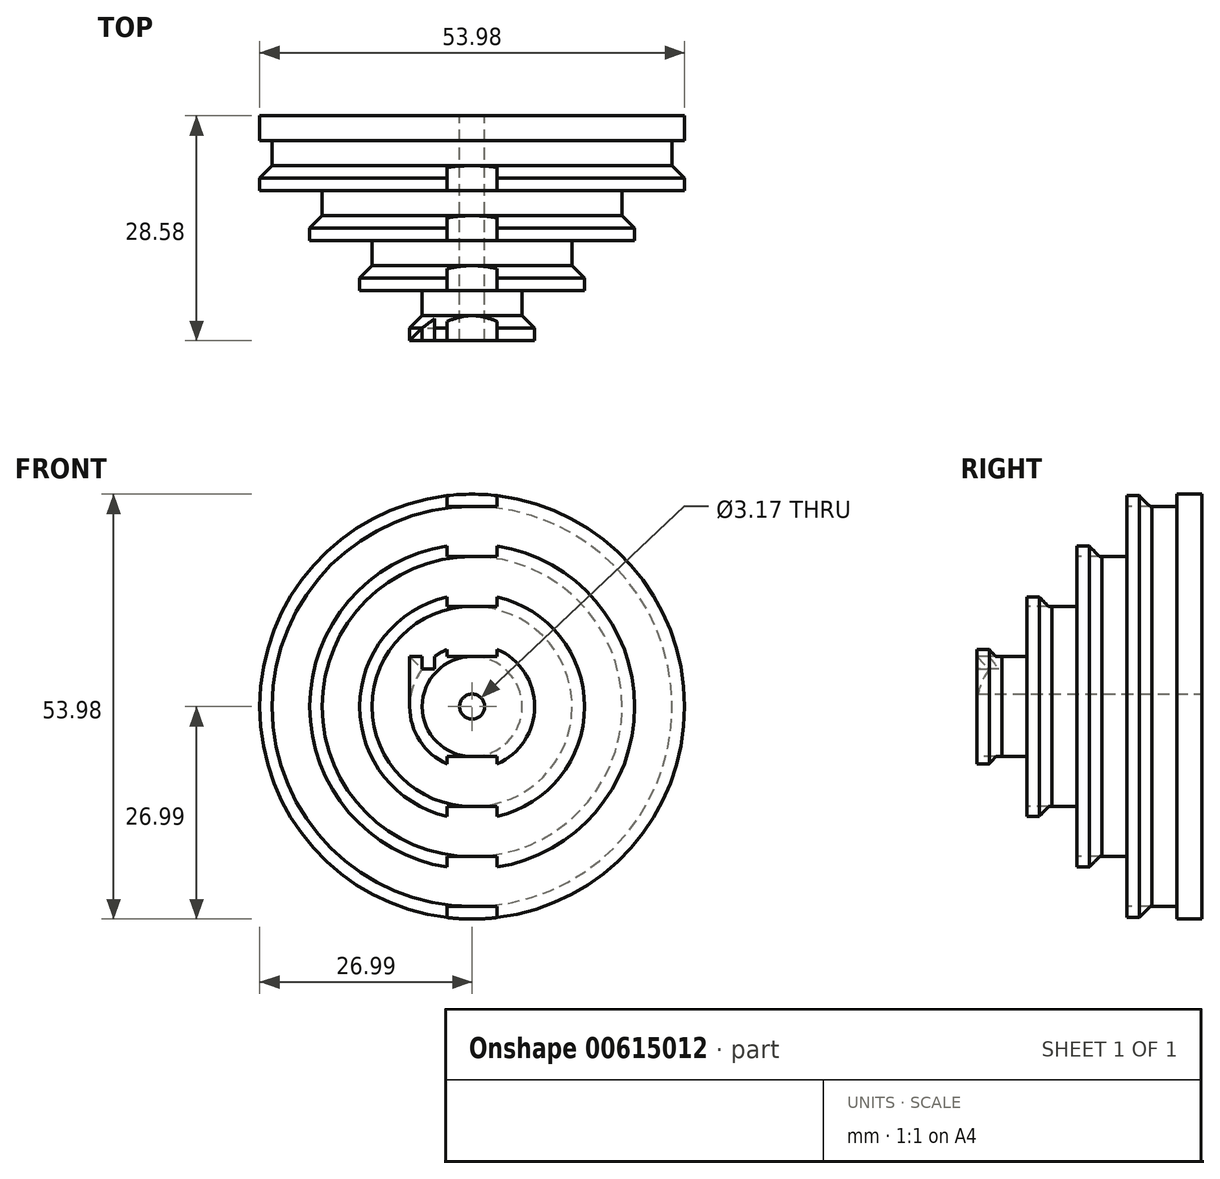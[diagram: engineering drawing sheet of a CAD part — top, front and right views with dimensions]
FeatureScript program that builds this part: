
annotation { "Feature Type Name" : "Feature", "Feature Type Description" : "" }
export const myFeature = defineFeature(function(context is Context, id is Id, definition is map)
    precondition{}
    {
        {
            var Q0;
            Q0=qCreatedBy(makeId("Front.planeOp"),FACE);
            var sketch = newSketch(context, id + "F0", { "sketchPlane" : qUnion([Q0])});
            skCircle(sketch, "E0", {"center": v(0, 0) * mm, "radius": 26.99 * mm});
            skSolve(sketch);
        }
        {
            var Q0;
            Q0=makeQuery(id+"F0.imprint","IMPRINT",FACE,{"disambiguationData":[TD([[makeQuery(id+"F0.imprint","IMPRINT",EDGE,{"derivedFrom":sQuery(id+"F0.wireOp",EDGE,"E0")}),1.0]])]});
            extrude(context, id + "F1", {"entities" : qUnion([Q0]), "depth" : 3.17 * mm, "offsetDistance" : 25.4 * mm});
        }
        {
            var Q0;
            Q0=makeQuery(id+"F1.opExtrude","CAP_FACE",FACE,{"disambiguationData":[OSD([sQuery(id+"F0.wireOp",EDGE,"E0")])],"isStart":false});
            var sketch = newSketch(context, id + "F2", { "sketchPlane" : qUnion([Q0])});
            skCircle(sketch, "E1", {"center": v(0, 0) * mm, "radius": 25.4 * mm});
            skSolve(sketch);
        }
        {
            var Q0;
            Q0=makeQuery(id+"F2.imprint","IMPRINT",FACE,{"disambiguationData":[TD([[makeQuery(id+"F2.imprint","IMPRINT",EDGE,{"derivedFrom":sQuery(id+"F2.wireOp",EDGE,"E1")}),1.0]])]});
            extrude(context, id + "F3", {"entities" : qUnion([Q0]), "operationType" : NewBodyOperationType.ADD, "depth" : 3.17 * mm, "offsetDistance" : 25.4 * mm});
        }
        {
            var Q0;
            Q0=makeQuery(id+"F3.opExtrude","CAP_FACE",FACE,{"disambiguationData":[OSD([sQuery(id+"F2.wireOp",EDGE,"E1")])],"isStart":false});
            var sketch = newSketch(context, id + "F4", { "sketchPlane" : qUnion([Q0])});
            skCircle(sketch, "E2", {"center": v(0, 0) * mm, "radius": 26.99 * mm});
            skSolve(sketch);
        }
        {
            var Q0;
            Q0=makeQuery(id+"F4.imprint","IMPRINT",FACE,{"disambiguationData":[TD([[makeQuery(id+"F4.imprint","IMPRINT",EDGE,{"derivedFrom":sQuery(id+"F4.wireOp",EDGE,"E2")}),1.0]])]});
            var Q1;
            Q1=makeQuery(id+"F4.imprint","IMPRINT",FACE,{"disambiguationData":[TD([[makeQuery(id+"F4.imprint","IMPRINT",EDGE,{"derivedFrom":makeQuery(id+"F3.opExtrude","CAP_EDGE",EDGE,{"disambiguationData":[OSD([sQuery(id+"F2.wireOp",EDGE,"E1")])],"isStart":false})}),1.0]])]});
            extrude(context, id + "F5", {"entities" : qUnion([Q0, Q1]), "operationType" : NewBodyOperationType.ADD, "depth" : 3.17 * mm, "offsetDistance" : 25.4 * mm});
        }
        {
            var Q0;
            Q0=makeQuery(id+"F5.opExtrude","CAP_FACE",FACE,{"disambiguationData":[OSD([sQuery(id+"F4.wireOp",EDGE,"E2")])],"isStart":false});
            var sketch = newSketch(context, id + "F6", { "sketchPlane" : qUnion([Q0])});
            skLineSegment(sketch, "E3.bottom", {"start": v(3.17, 25.4) * mm, "end": v(-3.18, 25.4) * mm});
            skLineSegment(sketch, "E3.top", {"start": v(3.17, 28.57) * mm, "end": v(-3.18, 28.57) * mm});
            skLineSegment(sketch, "E3.left", {"start": v(3.17, 25.4) * mm, "end": v(3.17, 28.57) * mm});
            skLineSegment(sketch, "E3.right", {"start": v(-3.18, 25.4) * mm, "end": v(-3.18, 28.57) * mm});
            skPoint(sketch, "E3.middle", {"position": v(0, 26.99) * mm});
            skSolve(sketch);
        }
        {
            var Q0;
            Q0 = qSketchRegion(id + "F6", true);
            extrude(context, id + "F7", {"entities" : qUnion([Q0]), "operationType" : NewBodyOperationType.REMOVE, "oppositeDirection" : true, "depth" : 3.17 * mm, "offsetDistance" : 25.4 * mm});
        }
        {
            var Q0;
            Q0=makeQuery(id+"F5.opExtrude","CAP_FACE",FACE,{"disambiguationData":[OSD([sQuery(id+"F4.wireOp",EDGE,"E2")])],"isStart":false});
            var sketch = newSketch(context, id + "F8", { "sketchPlane" : qUnion([Q0])});
            skCircle(sketch, "E4", {"center": v(0, 0) * mm, "radius": 19.05 * mm});
            skSolve(sketch);
        }
        {
            var Q0;
            Q0 = qSketchRegion(id + "F8", true);
            extrude(context, id + "F9", {"entities" : qUnion([Q0]), "operationType" : NewBodyOperationType.ADD, "depth" : 3.17 * mm, "offsetDistance" : 25.4 * mm});
        }
        {
            var Q0;
            Q0=makeQuery(id+"F9.opExtrude","CAP_FACE",FACE,{"disambiguationData":[OSD([sQuery(id+"F8.wireOp",EDGE,"E4")])],"isStart":false});
            var sketch = newSketch(context, id + "F10", { "sketchPlane" : qUnion([Q0])});
            skCircle(sketch, "E5", {"center": v(0, 0) * mm, "radius": 20.64 * mm});
            skSolve(sketch);
        }
        {
            var Q0;
            Q0 = qSketchRegion(id + "F10", true);
            extrude(context, id + "F11", {"entities" : qUnion([Q0]), "operationType" : NewBodyOperationType.ADD, "depth" : 3.17 * mm, "offsetDistance" : 25.4 * mm});
        }
        {
            var Q0;
            Q0=makeQuery(id+"F11.opExtrude","CAP_FACE",FACE,{"disambiguationData":[OSD([sQuery(id+"F10.wireOp",EDGE,"E5")])],"isStart":false});
            var sketch = newSketch(context, id + "F12", { "sketchPlane" : qUnion([Q0])});
            skLineSegment(sketch, "E6.bottom", {"start": v(3.18, 19.05) * mm, "end": v(-3.17, 19.05) * mm});
            skLineSegment(sketch, "E6.top", {"start": v(3.18, 22.23) * mm, "end": v(-3.17, 22.23) * mm});
            skLineSegment(sketch, "E6.left", {"start": v(3.18, 19.05) * mm, "end": v(3.18, 22.23) * mm});
            skLineSegment(sketch, "E6.right", {"start": v(-3.17, 19.05) * mm, "end": v(-3.17, 22.23) * mm});
            skPoint(sketch, "E6.middle", {"position": v(0, 20.64) * mm});
            skSolve(sketch);
        }
        {
            var Q0;
            Q0 = qSketchRegion(id + "F12", true);
            extrude(context, id + "F13", {"entities" : qUnion([Q0]), "operationType" : NewBodyOperationType.REMOVE, "oppositeDirection" : true, "depth" : 3.17 * mm, "offsetDistance" : 25.4 * mm});
        }
        {
            var Q0;
            Q0=makeQuery(id+"F5.opExtrude","CAP_FACE",FACE,{"disambiguationData":[OSD([sQuery(id+"F4.wireOp",EDGE,"E2")])],"isStart":false});
            var sketch = newSketch(context, id + "F14", { "sketchPlane" : qUnion([Q0])});
            skLineSegment(sketch, "E7.bottom", {"start": v(3.18, -25.4) * mm, "end": v(-3.17, -25.4) * mm});
            skLineSegment(sketch, "E7.top", {"start": v(3.18, -28.57) * mm, "end": v(-3.17, -28.57) * mm});
            skLineSegment(sketch, "E7.left", {"start": v(3.18, -25.4) * mm, "end": v(3.18, -28.57) * mm});
            skLineSegment(sketch, "E7.right", {"start": v(-3.17, -25.4) * mm, "end": v(-3.17, -28.57) * mm});
            skPoint(sketch, "E7.middle", {"position": v(0, -26.99) * mm});
            skSolve(sketch);
        }
        {
            var Q0;
            Q0 = qSketchRegion(id + "F14", true);
            extrude(context, id + "F15", {"entities" : qUnion([Q0]), "operationType" : NewBodyOperationType.REMOVE, "oppositeDirection" : true, "depth" : 3.17 * mm, "offsetDistance" : 25.4 * mm});
        }
        {
            var Q0;
            Q0=makeQuery(id+"F11.opExtrude","CAP_FACE",FACE,{"disambiguationData":[OSD([sQuery(id+"F10.wireOp",EDGE,"E5")])],"isStart":false});
            var sketch = newSketch(context, id + "F16", { "sketchPlane" : qUnion([Q0])});
            skLineSegment(sketch, "E8.bottom", {"start": v(3.18, -19.05) * mm, "end": v(-3.17, -19.05) * mm});
            skLineSegment(sketch, "E8.top", {"start": v(3.18, -22.23) * mm, "end": v(-3.17, -22.23) * mm});
            skLineSegment(sketch, "E8.left", {"start": v(3.18, -19.05) * mm, "end": v(3.18, -22.23) * mm});
            skLineSegment(sketch, "E8.right", {"start": v(-3.17, -19.05) * mm, "end": v(-3.17, -22.23) * mm});
            skPoint(sketch, "E8.middle", {"position": v(0, -20.64) * mm});
            skSolve(sketch);
        }
        {
            var Q0;
            Q0 = qSketchRegion(id + "F16", true);
            extrude(context, id + "F17", {"entities" : qUnion([Q0]), "operationType" : NewBodyOperationType.REMOVE, "oppositeDirection" : true, "depth" : 3.17 * mm, "offsetDistance" : 25.4 * mm});
        }
        {
            var Q0;
            Q0=makeQuery(id+"F11.opExtrude","CAP_FACE",FACE,{"disambiguationData":[OSD([sQuery(id+"F10.wireOp",EDGE,"E5")])],"isStart":false});
            var sketch = newSketch(context, id + "F18", { "sketchPlane" : qUnion([Q0])});
            skCircle(sketch, "E9", {"center": v(0, 0) * mm, "radius": 12.7 * mm});
            skSolve(sketch);
        }
        {
            var Q0;
            Q0 = qSketchRegion(id + "F18", true);
            extrude(context, id + "F19", {"entities" : qUnion([Q0]), "operationType" : NewBodyOperationType.ADD, "depth" : 3.17 * mm, "offsetDistance" : 25.4 * mm});
        }
        {
            var Q0;
            Q0=makeQuery(id+"F19.opExtrude","CAP_FACE",FACE,{"disambiguationData":[OSD([sQuery(id+"F18.wireOp",EDGE,"E9")])],"isStart":false});
            var sketch = newSketch(context, id + "F20", { "sketchPlane" : qUnion([Q0])});
            skCircle(sketch, "E10", {"center": v(0, 0) * mm, "radius": 14.29 * mm});
            skSolve(sketch);
        }
        {
            var Q0;
            Q0 = qSketchRegion(id + "F20", true);
            extrude(context, id + "F21", {"entities" : qUnion([Q0]), "operationType" : NewBodyOperationType.ADD, "depth" : 3.17 * mm, "offsetDistance" : 25.4 * mm});
        }
        {
            var Q0;
            Q0=makeQuery(id+"F21.opExtrude","CAP_FACE",FACE,{"disambiguationData":[OSD([sQuery(id+"F20.wireOp",EDGE,"E10")])],"isStart":false});
            var sketch = newSketch(context, id + "F22", { "sketchPlane" : qUnion([Q0])});
            skLineSegment(sketch, "E11.bottom", {"start": v(3.17, 15.88) * mm, "end": v(-3.18, 15.88) * mm});
            skLineSegment(sketch, "E11.top", {"start": v(3.17, 12.7) * mm, "end": v(-3.18, 12.7) * mm});
            skLineSegment(sketch, "E11.left", {"start": v(3.17, 15.88) * mm, "end": v(3.17, 12.7) * mm});
            skLineSegment(sketch, "E11.right", {"start": v(-3.18, 15.88) * mm, "end": v(-3.18, 12.7) * mm});
            skPoint(sketch, "E11.middle", {"position": v(0, 14.29) * mm});
            skSolve(sketch);
        }
        {
            var Q0;
            Q0 = qSketchRegion(id + "F22", true);
            extrude(context, id + "F23", {"entities" : qUnion([Q0]), "operationType" : NewBodyOperationType.REMOVE, "oppositeDirection" : true, "depth" : 3.17 * mm, "offsetDistance" : 25.4 * mm});
        }
        {
            var Q0;
            Q0=makeQuery(id+"F21.opExtrude","CAP_FACE",FACE,{"disambiguationData":[OSD([sQuery(id+"F20.wireOp",EDGE,"E10")])],"isStart":false});
            var sketch = newSketch(context, id + "F24", { "sketchPlane" : qUnion([Q0])});
            skLineSegment(sketch, "E12.bottom", {"start": v(3.18, -12.7) * mm, "end": v(-3.17, -12.7) * mm});
            skLineSegment(sketch, "E12.top", {"start": v(3.18, -15.88) * mm, "end": v(-3.17, -15.88) * mm});
            skLineSegment(sketch, "E12.left", {"start": v(3.18, -12.7) * mm, "end": v(3.18, -15.88) * mm});
            skLineSegment(sketch, "E12.right", {"start": v(-3.17, -12.7) * mm, "end": v(-3.17, -15.88) * mm});
            skPoint(sketch, "E12.middle", {"position": v(0, -14.29) * mm});
            skSolve(sketch);
        }
        {
            var Q0;
            Q0 = qSketchRegion(id + "F24", true);
            extrude(context, id + "F25", {"entities" : qUnion([Q0]), "operationType" : NewBodyOperationType.REMOVE, "oppositeDirection" : true, "depth" : 3.17 * mm, "offsetDistance" : 25.4 * mm});
        }
        {
            var Q0;
            Q0=makeQuery(id+"F21.opExtrude","CAP_FACE",FACE,{"disambiguationData":[OSD([sQuery(id+"F20.wireOp",EDGE,"E10")])],"isStart":false});
            var sketch = newSketch(context, id + "F26", { "sketchPlane" : qUnion([Q0])});
            skCircle(sketch, "E13", {"center": v(0, 0) * mm, "radius": 6.35 * mm});
            skSolve(sketch);
        }
        {
            var Q0;
            Q0 = qSketchRegion(id + "F26", true);
            extrude(context, id + "F27", {"entities" : qUnion([Q0]), "operationType" : NewBodyOperationType.ADD, "depth" : 3.17 * mm, "offsetDistance" : 25.4 * mm});
        }
        {
            var Q0;
            Q0=makeQuery(id+"F27.opExtrude","CAP_FACE",FACE,{"disambiguationData":[OSD([sQuery(id+"F26.wireOp",EDGE,"E13")])],"isStart":false});
            var sketch = newSketch(context, id + "F28", { "sketchPlane" : qUnion([Q0])});
            skCircle(sketch, "E14", {"center": v(0, 0) * mm, "radius": 7.94 * mm});
            skSolve(sketch);
        }
        {
            var Q0;
            Q0 = qSketchRegion(id + "F28", true);
            extrude(context, id + "F29", {"entities" : qUnion([Q0]), "operationType" : NewBodyOperationType.ADD, "depth" : 3.17 * mm, "offsetDistance" : 25.4 * mm});
        }
        {
            var Q0;
            Q0=makeQuery(id+"F29.opExtrude","CAP_FACE",FACE,{"disambiguationData":[OSD([sQuery(id+"F28.wireOp",EDGE,"E14")])],"isStart":false});
            var sketch = newSketch(context, id + "F30", { "sketchPlane" : qUnion([Q0])});
            skLineSegment(sketch, "E15.bottom", {"start": v(3.17, 6.35) * mm, "end": v(-3.18, 6.35) * mm});
            skLineSegment(sketch, "E15.top", {"start": v(3.18, 9.53) * mm, "end": v(-3.17, 9.53) * mm});
            skLineSegment(sketch, "E15.left", {"start": v(3.17, 6.35) * mm, "end": v(3.18, 9.53) * mm});
            skLineSegment(sketch, "E15.right", {"start": v(-3.18, 6.35) * mm, "end": v(-3.17, 9.53) * mm});
            skPoint(sketch, "E15.middle", {"position": v(0, 7.94) * mm});
            skSolve(sketch);
        }
        {
            var Q0;
            Q0 = qSketchRegion(id + "F30", true);
            extrude(context, id + "F31", {"entities" : qUnion([Q0]), "operationType" : NewBodyOperationType.REMOVE, "oppositeDirection" : true, "depth" : 3.17 * mm, "offsetDistance" : 25.4 * mm});
        }
        {
            var Q0;
            Q0=makeQuery(id+"F29.opExtrude","CAP_FACE",FACE,{"disambiguationData":[OSD([sQuery(id+"F28.wireOp",EDGE,"E14")])],"isStart":false});
            var sketch = newSketch(context, id + "F32", { "sketchPlane" : qUnion([Q0])});
            skLineSegment(sketch, "E16.bottom", {"start": v(3.18, -6.35) * mm, "end": v(-3.17, -6.35) * mm});
            skLineSegment(sketch, "E16.top", {"start": v(3.18, -9.53) * mm, "end": v(-3.17, -9.53) * mm});
            skLineSegment(sketch, "E16.left", {"start": v(3.18, -6.35) * mm, "end": v(3.18, -9.53) * mm});
            skLineSegment(sketch, "E16.right", {"start": v(-3.17, -6.35) * mm, "end": v(-3.17, -9.53) * mm});
            skPoint(sketch, "E16.middle", {"position": v(0, -7.94) * mm});
            skSolve(sketch);
        }
        {
            var Q0;
            Q0 = qSketchRegion(id + "F32", true);
            extrude(context, id + "F33", {"entities" : qUnion([Q0]), "operationType" : NewBodyOperationType.REMOVE, "oppositeDirection" : true, "depth" : 3.17 * mm, "offsetDistance" : 25.4 * mm});
        }
        {
            var Q0;
            Q0=makeQuery(id+"F1.opExtrude","CAP_FACE",FACE,{"disambiguationData":[OSD([sQuery(id+"F0.wireOp",EDGE,"E0")])],"isStart":true});
            var sketch = newSketch(context, id + "F34", { "sketchPlane" : qUnion([Q0])});
            skCircle(sketch, "E17", {"center": v(0, 0) * mm, "radius": 1.59 * mm});
            skSolve(sketch);
        }
        {
            var Q0;
            Q0 = qSketchRegion(id + "F34", true);
            extrude(context, id + "F35", {"entities" : qUnion([Q0]), "operationType" : NewBodyOperationType.REMOVE, "oppositeDirection" : true, "depth" : 28.57 * mm, "offsetDistance" : 25.4 * mm});
        }
        {
            var Q0;
            {var subQ0=sQuery(id+"F4.wireOp",EDGE,"E2");Q0=makeQuery(id+"F15.boolean.opBoolean","SPLIT",EDGE,{"disambiguationData":[TD([makeQuery(id+"F7.boolean.opBoolean","COPY",FACE,{"derivedFrom":makeQuery(id+"F7.opExtrude","SWEPT_FACE",FACE,{"disambiguationData":[OSD([sQuery(id+"F6.wireOp",EDGE,"E3.left")])]})})])],"derivedFrom":makeQuery(id+"F5.opExtrude","CAP_EDGE",EDGE,{"disambiguationData":[OSD([subQ0])],"isStart":true})});}
            var Q1;
            {var subQ0=sQuery(id+"F4.wireOp",EDGE,"E2");Q1=makeQuery(id+"F15.boolean.opBoolean","SPLIT",EDGE,{"disambiguationData":[TD([makeQuery(id+"F7.boolean.opBoolean","COPY",FACE,{"derivedFrom":makeQuery(id+"F7.opExtrude","SWEPT_FACE",FACE,{"disambiguationData":[OSD([sQuery(id+"F6.wireOp",EDGE,"E3.right")])]})})])],"derivedFrom":makeQuery(id+"F5.opExtrude","CAP_EDGE",EDGE,{"disambiguationData":[OSD([subQ0])],"isStart":true})});}
            var Q2;
            {var subQ0=sQuery(id+"F10.wireOp",EDGE,"E5");Q2=makeQuery(id+"F17.boolean.opBoolean","SPLIT",EDGE,{"disambiguationData":[TD([makeQuery(id+"F13.boolean.opBoolean","COPY",FACE,{"derivedFrom":makeQuery(id+"F13.opExtrude","SWEPT_FACE",FACE,{"disambiguationData":[OSD([sQuery(id+"F12.wireOp",EDGE,"E6.left")])]})})])],"derivedFrom":makeQuery(id+"F11.opExtrude","CAP_EDGE",EDGE,{"disambiguationData":[OSD([subQ0])],"isStart":true})});}
            var Q3;
            {var subQ0=sQuery(id+"F10.wireOp",EDGE,"E5");Q3=makeQuery(id+"F17.boolean.opBoolean","SPLIT",EDGE,{"disambiguationData":[TD([makeQuery(id+"F13.boolean.opBoolean","COPY",FACE,{"derivedFrom":makeQuery(id+"F13.opExtrude","SWEPT_FACE",FACE,{"disambiguationData":[OSD([sQuery(id+"F12.wireOp",EDGE,"E6.right")])]})})])],"derivedFrom":makeQuery(id+"F11.opExtrude","CAP_EDGE",EDGE,{"disambiguationData":[OSD([subQ0])],"isStart":true})});}
            chamfer(context, id + "F36", {"entities" : qUnion([Q0, Q1, Q2, Q3]), "width" : 1.59 * mm, "tangentPropagation" : true});
        }
        {
            var Q0;
            Q0=makeQuery(id+"F29.opExtrude","CAP_FACE",FACE,{"disambiguationData":[OSD([sQuery(id+"F28.wireOp",EDGE,"E14")])],"isStart":false});
            var sketch = newSketch(context, id + "F37", { "sketchPlane" : qUnion([Q0])});
            skLineSegment(sketch, "E18.bottom", {"start": v(-7.94, 0) * mm, "end": v(-6.35, 0) * mm});
            skLineSegment(sketch, "E18.top", {"start": v(-7.94, 6.35) * mm, "end": v(-6.35, 6.35) * mm});
            skLineSegment(sketch, "E18.left", {"start": v(-7.94, 0) * mm, "end": v(-7.94, 6.35) * mm});
            skLineSegment(sketch, "E18.right", {"start": v(-6.35, 0) * mm, "end": v(-6.35, 6.35) * mm});
            skSolve(sketch);
        }
        {
            var Q0;
            Q0 = qSketchRegion(id + "F37", true);
            extrude(context, id + "F38", {"entities" : qUnion([Q0]), "operationType" : NewBodyOperationType.ADD, "oppositeDirection" : true, "depth" : 1.59 * mm, "offsetDistance" : 25.4 * mm});
        }
        {
            var Q0;
            {var subQ0=sQuery(id+"F20.wireOp",EDGE,"E10");Q0=makeQuery(id+"F25.boolean.opBoolean","SPLIT",EDGE,{"disambiguationData":[TD([makeQuery(id+"F23.boolean.opBoolean","COPY",FACE,{"derivedFrom":makeQuery(id+"F23.opExtrude","SWEPT_FACE",FACE,{"disambiguationData":[OSD([sQuery(id+"F22.wireOp",EDGE,"E11.right")])]})})])],"derivedFrom":makeQuery(id+"F21.opExtrude","CAP_EDGE",EDGE,{"disambiguationData":[OSD([subQ0])],"isStart":true})});}
            var Q1;
            {var subQ0=sQuery(id+"F20.wireOp",EDGE,"E10");Q1=makeQuery(id+"F25.boolean.opBoolean","SPLIT",EDGE,{"disambiguationData":[TD([makeQuery(id+"F23.boolean.opBoolean","COPY",FACE,{"derivedFrom":makeQuery(id+"F23.opExtrude","SWEPT_FACE",FACE,{"disambiguationData":[OSD([sQuery(id+"F22.wireOp",EDGE,"E11.left")])]})})])],"derivedFrom":makeQuery(id+"F21.opExtrude","CAP_EDGE",EDGE,{"disambiguationData":[OSD([subQ0])],"isStart":true})});}
            var Q2;
            {var subQ0=sQuery(id+"F28.wireOp",EDGE,"E14");Q2=makeQuery(id+"F33.boolean.opBoolean","SPLIT",EDGE,{"disambiguationData":[TD([makeQuery(id+"F31.boolean.opBoolean","COPY",FACE,{"derivedFrom":makeQuery(id+"F31.opExtrude","SWEPT_FACE",FACE,{"disambiguationData":[OSD([sQuery(id+"F30.wireOp",EDGE,"E15.left")])]})})])],"derivedFrom":makeQuery(id+"F29.opExtrude","CAP_EDGE",EDGE,{"disambiguationData":[OSD([subQ0])],"isStart":true})});}
            chamfer(context, id + "F39", {"entities" : qUnion([Q0, Q1, Q2]), "width" : 1.59 * mm, "tangentPropagation" : true});
        }
        {
            var Q0;
            Q0=makeQuery(id+"F38.boolean.opBoolean","MERGE",FACE,{"derivedFrom":[makeQuery(id+"F29.opExtrude","CAP_FACE",FACE,{"disambiguationData":[OSD([sQuery(id+"F28.wireOp",EDGE,"E14")])],"isStart":false}),makeQuery(id+"F38.opExtrude","CAP_FACE",FACE,{"disambiguationData":[OSD([sQuery(id+"F37.wireOp",EDGE,"E18.bottom"),sQuery(id+"F37.wireOp",EDGE,"E18.top"),sQuery(id+"F37.wireOp",EDGE,"E18.left"),sQuery(id+"F37.wireOp",EDGE,"E18.right")])],"isStart":true})]});
            var sketch = newSketch(context, id + "F40", { "sketchPlane" : qUnion([Q0])});
            skLineSegment(sketch, "E19.bottom", {"start": v(-6.35, 6.35) * mm, "end": v(-4.76, 6.35) * mm});
            skLineSegment(sketch, "E19.top", {"start": v(-6.35, 4.76) * mm, "end": v(-4.76, 4.76) * mm});
            skLineSegment(sketch, "E19.left", {"start": v(-6.35, 6.35) * mm, "end": v(-6.35, 4.76) * mm});
            skLineSegment(sketch, "E19.right", {"start": v(-4.76, 6.35) * mm, "end": v(-4.76, 4.76) * mm});
            skSolve(sketch);
        }
        {
            var Q0;
            Q0 = qSketchRegion(id + "F40", true);
            extrude(context, id + "F41", {"entities" : qUnion([Q0]), "operationType" : NewBodyOperationType.REMOVE, "oppositeDirection" : true, "depth" : 3.17 * mm, "offsetDistance" : 25.4 * mm});
        }
        {
            var Q0;
            {var subQ0=sQuery(id+"F28.wireOp",EDGE,"E14");var subQ3=makeQuery(id+"F33.opExtrude","SWEPT_FACE",FACE,{"disambiguationData":[OSD([sQuery(id+"F32.wireOp",EDGE,"E16.right")])]});Q0=makeQuery(id+"F41.boolean.opBoolean","SPLIT",EDGE,{"disambiguationData":[TD([makeQuery(id+"F33.boolean.opBoolean","COPY",FACE,{"derivedFrom":subQ3})])],"derivedFrom":makeQuery(id+"F33.boolean.opBoolean","SPLIT",EDGE,{"disambiguationData":[TD([makeQuery(id+"F31.boolean.opBoolean","COPY",FACE,{"derivedFrom":makeQuery(id+"F31.opExtrude","SWEPT_FACE",FACE,{"disambiguationData":[OSD([sQuery(id+"F30.wireOp",EDGE,"E15.right")])]})})])],"derivedFrom":makeQuery(id+"F29.opExtrude","CAP_EDGE",EDGE,{"disambiguationData":[OSD([subQ0])],"isStart":true})})});}
            var Q1;
            {var subQ0=sQuery(id+"F28.wireOp",EDGE,"E14");var subQ3=makeQuery(id+"F31.boolean.opBoolean","COPY",FACE,{"derivedFrom":makeQuery(id+"F31.opExtrude","SWEPT_FACE",FACE,{"disambiguationData":[OSD([sQuery(id+"F30.wireOp",EDGE,"E15.right")])]})});Q1=makeQuery(id+"F41.boolean.opBoolean","SPLIT",EDGE,{"disambiguationData":[TD([subQ3])],"derivedFrom":makeQuery(id+"F33.boolean.opBoolean","SPLIT",EDGE,{"disambiguationData":[TD([subQ3])],"derivedFrom":makeQuery(id+"F29.opExtrude","CAP_EDGE",EDGE,{"disambiguationData":[OSD([subQ0])],"isStart":true})})});}
            chamfer(context, id + "F42", {"entities" : qUnion([Q0, Q1]), "width" : 1.59 * mm, "tangentPropagation" : true});
        }
        {
            var Q0;
            Q0=makeQuery(id+"F38.opExtrude","CAP_EDGE",EDGE,{"disambiguationData":[OSD([sQuery(id+"F37.wireOp",EDGE,"E18.left")])],"isStart":false});
            var Q1;
            Q1=makeQuery(id+"F38.opExtrude","CAP_EDGE",EDGE,{"disambiguationData":[OSD([sQuery(id+"F37.wireOp",EDGE,"E18.top")])],"isStart":false});
            chamfer(context, id + "F43", {"entities" : qUnion([Q0, Q1]), "width" : 1.59 * mm, "tangentPropagation" : true});
        }
    });
